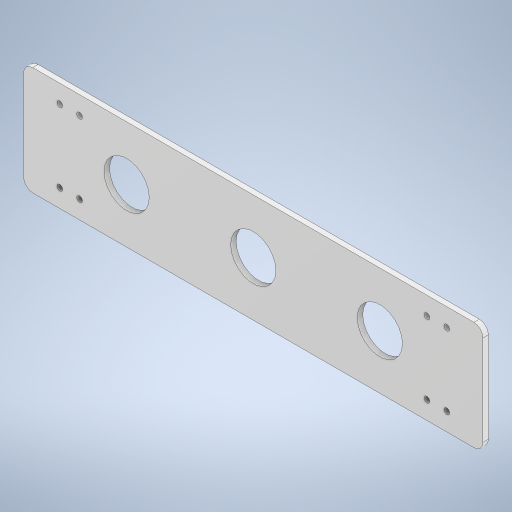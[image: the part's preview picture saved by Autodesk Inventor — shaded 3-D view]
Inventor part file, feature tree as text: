
AUTODESK INVENTOR PART (.ipt)
format: ipt  version: 2024.3 (Build 283343000, 343)  size: 321,024 bytes
history: native  units: mm
features: sketch x5, extrude x4, other x1, fillet x1, hole x1
ambient origin geometry x8: Origin, YZ Plane, XZ Plane, XY Plane, X Axis, Y Axis, Z Axis, Center Point
bodies: Body1 (feature_tree)
feature tree (12):
  other  "ソリッド1"
  extrude  "押し出し1"  Depth=260.0mm
  extrude  "押し出し3"  Depth=3.0mm
  extrude  "押し出し4"  Depth=60.0mm TaperAngle=0.0deg
  extrude  "押し出し7"  Depth=25.0mm
  fillet  "フィレット1"  Radius=25.0mm
  hole  "穴1"  [1 undecoded]
  sketch  "スケッチ1"
  sketch  "スケッチ3"
  sketch  "スケッチ5"
  sketch  "スケッチ8"
  sketch  "スケッチ13"
note: 1 required parameter value undecoded (feature->parameter linkage not recoverable at this tier; creation-order binding heuristic only, values carry confidence <= 0.55)
